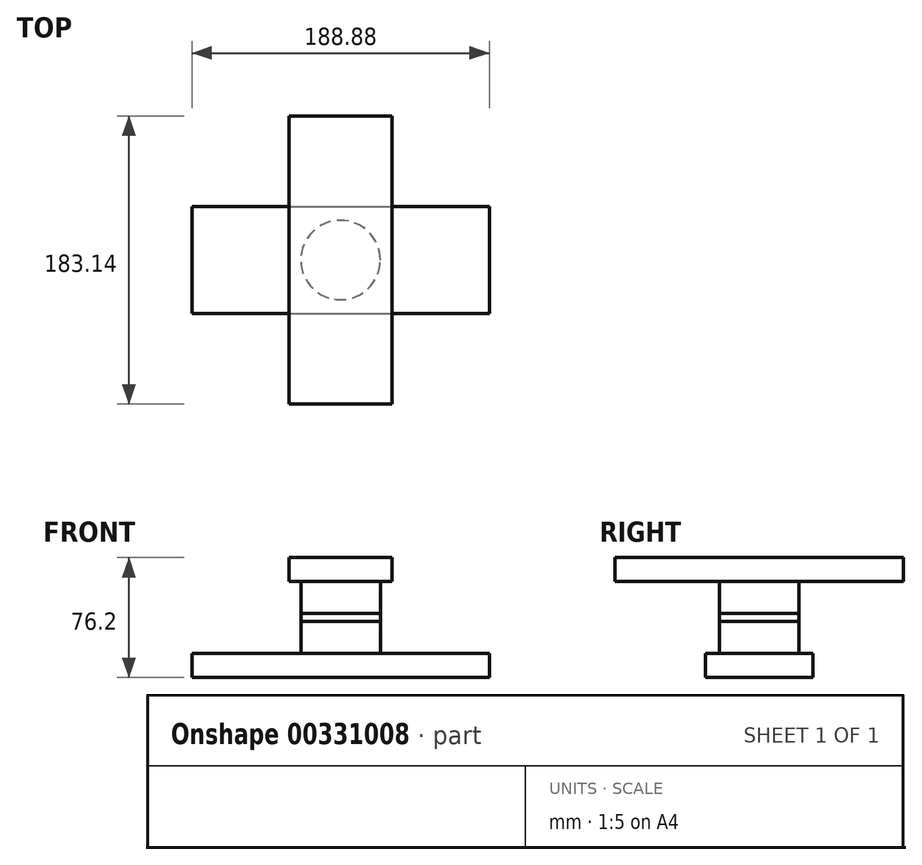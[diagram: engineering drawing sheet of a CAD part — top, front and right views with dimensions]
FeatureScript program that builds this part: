
annotation { "Feature Type Name" : "Feature", "Feature Type Description" : "" }
export const myFeature = defineFeature(function(context is Context, id is Id, definition is map)
    precondition{}
    {
        {
            var Q0;
            Q0=qCreatedBy(makeId("Top.planeOp"),FACE);
            var sketch = newSketch(context, id + "F0", { "sketchPlane" : qUnion([Q0])});
            skLineSegment(sketch, "E0.bottom", {"start": v(-94.44, 34.12) * mm, "end": v(94.44, 34.12) * mm});
            skLineSegment(sketch, "E0.top", {"start": v(-94.44, -34.12) * mm, "end": v(94.44, -34.12) * mm});
            skLineSegment(sketch, "E0.left", {"start": v(-94.44, 34.12) * mm, "end": v(-94.44, -34.12) * mm});
            skLineSegment(sketch, "E0.right", {"start": v(94.44, 34.12) * mm, "end": v(94.44, -34.12) * mm});
            skPoint(sketch, "E0.middle", {"position": v(0, 0) * mm});
            skSolve(sketch);
        }
        {
            var Q0;
            Q0 = qSketchRegion(id + "F0", true);
            extrude(context, id + "F1", {"entities" : qUnion([Q0]), "depth" : 15.24 * mm});
        }
        {
            var Q0;
            Q0=makeQuery(id+"F1.opExtrude","CAP_FACE",FACE,{"disambiguationData":[OSD([sQuery(id+"F0.wireOp",EDGE,"E0.bottom"),sQuery(id+"F0.wireOp",EDGE,"E0.top"),sQuery(id+"F0.wireOp",EDGE,"E0.left"),sQuery(id+"F0.wireOp",EDGE,"E0.right")])],"isStart":false});
            var sketch = newSketch(context, id + "F2", { "sketchPlane" : qUnion([Q0])});
            skCircle(sketch, "E1", {"center": v(0, 0) * mm, "radius": 25.23 * mm});
            skSolve(sketch);
        }
        {
            var Q0;
            Q0=makeQuery(id+"F2.imprint","IMPRINT",FACE,{"disambiguationData":[TD([[makeQuery(id+"F2.imprint","IMPRINT",EDGE,{"derivedFrom":sQuery(id+"F2.wireOp",EDGE,"E1")}),1.0]])]});
            extrude(context, id + "F3", {"entities" : qUnion([Q0]), "depth" : 20.32 * mm});
        }
        {
            var Q0;
            Q0=makeQuery(id+"F3.opExtrude","CAP_FACE",FACE,{"disambiguationData":[OSD([sQuery(id+"F2.wireOp",EDGE,"E1")])],"isStart":false});
            extrude(context, id + "F4", {"entities" : qUnion([Q0]), "depth" : 5.08 * mm});
        }
        {
            var Q0;
            Q0=makeQuery(id+"F4.opExtrude","CAP_FACE",FACE,{"disambiguationData":[OSD([sQuery(id+"F2.wireOp",EDGE,"E1")])],"isStart":false});
            extrude(context, id + "F5", {"entities" : qUnion([Q0]), "depth" : 20.32 * mm});
        }
        {
            var Q0;
            Q0=makeQuery(id+"F5.opExtrude","CAP_FACE",FACE,{"disambiguationData":[OSD([sQuery(id+"F2.wireOp",EDGE,"E1")])],"isStart":false});
            var sketch = newSketch(context, id + "F6", { "sketchPlane" : qUnion([Q0])});
            skLineSegment(sketch, "E2.bottom", {"start": v(32.7, 91.57) * mm, "end": v(-32.7, 91.57) * mm});
            skLineSegment(sketch, "E2.top", {"start": v(32.7, -91.57) * mm, "end": v(-32.7, -91.57) * mm});
            skLineSegment(sketch, "E2.left", {"start": v(32.7, 91.57) * mm, "end": v(32.7, -91.57) * mm});
            skLineSegment(sketch, "E2.right", {"start": v(-32.7, 91.57) * mm, "end": v(-32.7, -91.57) * mm});
            skPoint(sketch, "E2.middle", {"position": v(0, 0) * mm});
            skSolve(sketch);
        }
        {
            var Q0;
            Q0 = qSketchRegion(id + "F6", true);
            extrude(context, id + "F7", {"entities" : qUnion([Q0]), "depth" : 15.24 * mm});
        }
    });
